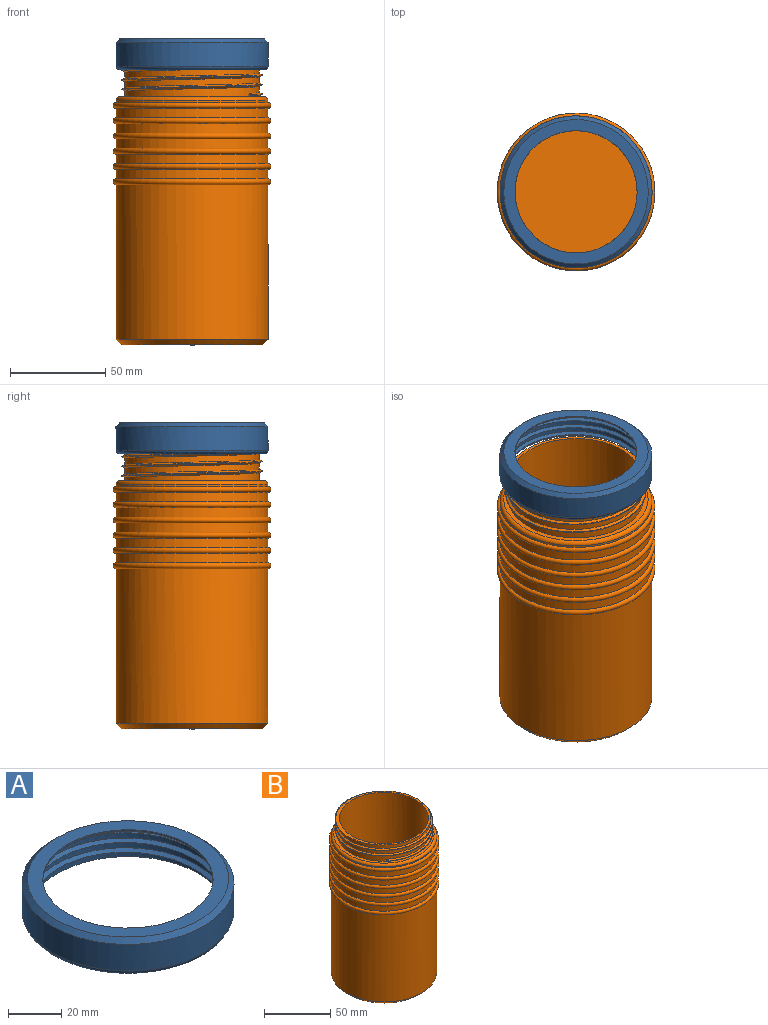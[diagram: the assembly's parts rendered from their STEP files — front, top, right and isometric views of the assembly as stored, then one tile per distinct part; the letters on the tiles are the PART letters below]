
ASSEMBLY  parts=2 mates=1
PART A: 13 faces, bbox 87.1x87.4x17.7 mm
  f0: plane 75.7x75.7mm, normal (0,0,1), area 1283.7mm2, adj f4,f12
  f1: cylinder r=37.45mm len=74.9mm, axis (0,0,-1), area 2082.9mm2, adj f2,f7,f8,f9,f10
  f2: plane 75.7x75.7mm, normal (0,0,-1), area 94.6mm2, adj f1,f11
  f3: cylinder r=39.85mm len=79.7mm, axis (0,0,-1), area 3054.7mm2, adj f11,f12
  f4: cylinder r=32mm len=64mm, axis (0,0,-1), area 140.7mm2, adj f0,f6
  f5: plane 74.78x74.03mm, normal (0,0,-1), area 934.9mm2, adj f6,f7,f9,f10
  f6: cone r=32mm half-angle=45deg, axis (0,0,-1), area 143.3mm2, adj f4,f5
  f7: cone r=36.95mm half-angle=45deg, axis (0,0,-1), area 107.1mm2, adj f1,f5,f9,f10
  f8: plane 1.86x1.18mm, normal (-0.73,0.68,0), area 1.5mm2, adj f1,f9,f10
  f9: bspline ~86.49x74.9mm, area 1380.3mm2, adj f1,f5,f7,f8,f10
  f10: bspline ~86.49x74.9mm, area 1293.7mm2, adj f1,f5,f7,f8,f9
  f11: torus R=37.85mm, axis (0,0,1), area 772.3mm2, adj f2,f3
  f12: cone r=39.85mm half-angle=45deg, axis (0,0,-1), area 690.4mm2, adj f0,f3
PART B: 25 faces, bbox 89.9x89.9x146.6 mm
  f0: cylinder r=35.35mm len=70.7mm, axis (0,0,-1), area 2165.2mm2, adj f1,f2,f18,f20,f21
  f1: bspline ~85.33x73.9mm, area 989.5mm2, adj f0,f3,f20,f21
  f2: bspline ~85.33x73.9mm, area 916.6mm2, adj f0,f3,f20,f21
  f3: bspline ~73.93x73.93mm, area 271.3mm2, adj f1,f2,f20,f21
  f4: cylinder r=39.85mm len=79.7mm, axis (0,0,-1), area 250.4mm2, adj f5,f19
  f5: torus R=39.85mm, axis (0,0,-1), area 1208.2mm2, adj f4,f6
  f6: cylinder r=39.85mm len=79.7mm, axis (0,0,-1), area 1251.9mm2, adj f5,f7
  f7: torus R=39.85mm, axis (0,0,-1), area 1208.2mm2, adj f6,f8
  f8: cylinder r=39.85mm len=79.7mm, axis (0,0,-1), area 1251.9mm2, adj f7,f9
  f9: torus R=39.85mm, axis (0,0,-1), area 1208.2mm2, adj f8,f10
  f10: cylinder r=39.85mm len=79.7mm, axis (0,0,-1), area 1251.9mm2, adj f9,f11
  f11: torus R=39.85mm, axis (0,0,-1), area 1208.2mm2, adj f10,f12
  f12: cylinder r=39.85mm len=79.7mm, axis (0,0,-1), area 1251.9mm2, adj f11,f13
  f13: torus R=39.85mm, axis (0,0,-1), area 1208.2mm2, adj f12,f14
  f14: cylinder r=39.85mm len=79.7mm, axis (0,0,-1), area 1251.9mm2, adj f13,f15
  f15: torus R=39.85mm, axis (0,0,-1), area 1208.2mm2, adj f14,f16
  f16: cylinder r=39.85mm len=81mm, axis (0,0,-1), area 20281.2mm2, adj f15,f24
  f17: cone r=39.85mm half-angle=89.9deg, axis (0,0,1), area 4266mm2, adj f24
  f18: plane 75.7x75.7mm, normal (0,0,1), area 575mm2, adj f0,f19
  f19: torus R=37.85mm, axis (0,0,-1), area 772.3mm2, adj f4,f18
  f20: plane 1.86x1.04mm, normal (-0.73,0.68,0), area 1.5mm2, adj f0,f1,f2,f3
  f21: plane 72.14x71.09mm, normal (0,0,1), area 444.3mm2, adj f0,f1,f2,f3,f23
  f22: plane 67.2x67.2mm, normal (0,0,1), area 3546.7mm2, adj f23
  f23: cylinder r=33.6mm len=142.09mm, axis (0,0,-1), area 29998mm2, adj f21,f22
  f24: cone r=36.85mm half-angle=45deg, axis (0,0,1), area 1022.9mm2, adj f16,f17
PLACE A rot(axis=(0,0,1),108.8deg) t=(-81.58,-11.58,3.01)mm
PLACE B rot(axis=(0,0,1),99.2deg) t=(-81.58,-11.58,18.25)mm fixed
MATE cylindrical B.f0 <-> A.f1  axis (0,0,-1) through (-81.58,-11.58,51.95)mm
